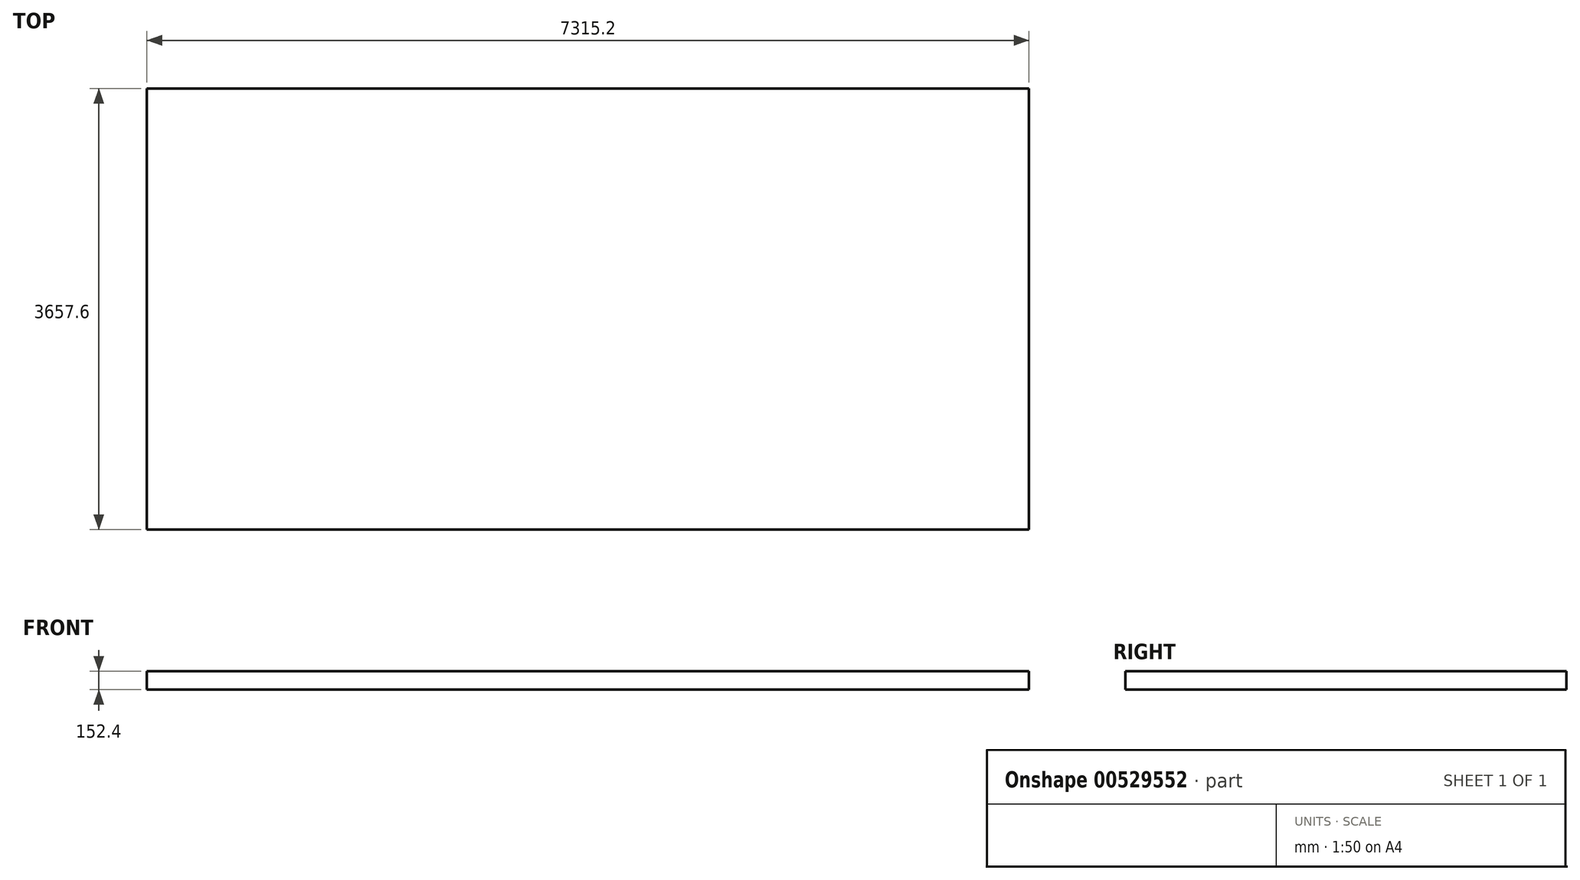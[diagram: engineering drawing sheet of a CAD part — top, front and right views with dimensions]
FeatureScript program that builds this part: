
annotation { "Feature Type Name" : "Feature", "Feature Type Description" : "" }
export const myFeature = defineFeature(function(context is Context, id is Id, definition is map)
    precondition{}
    {
        {
            var Q0;
            Q0=qCreatedBy(makeId("Top.planeOp"),FACE);
            var sketch = newSketch(context, id + "F0", { "sketchPlane" : qUnion([Q0])});
            skLineSegment(sketch, "E0.bottom", {"start": v(-3664.27, -2844.29) * mm, "end": v(3650.93, -2844.29) * mm});
            skLineSegment(sketch, "E0.top", {"start": v(-3664.27, 813.31) * mm, "end": v(3650.93, 813.31) * mm});
            skLineSegment(sketch, "E0.left", {"start": v(-3664.27, -2844.29) * mm, "end": v(-3664.27, 813.31) * mm});
            skLineSegment(sketch, "E0.right", {"start": v(3650.93, -2844.29) * mm, "end": v(3650.93, 813.31) * mm});
            skSolve(sketch);
        }
        {
            var Q0;
            Q0=makeQuery(id+"F0.imprint","IMPRINT",FACE,{"disambiguationData":[TD([[makeQuery(id+"F0.imprint","IMPRINT",EDGE,{"derivedFrom":sQuery(id+"F0.wireOp",EDGE,"E0.bottom")}),1.0]])]});
            extrude(context, id + "F1", {"entities" : qUnion([Q0]), "depth" : 152.4 * mm, "offsetDistance" : 30.48 * mm});
        }
    });
